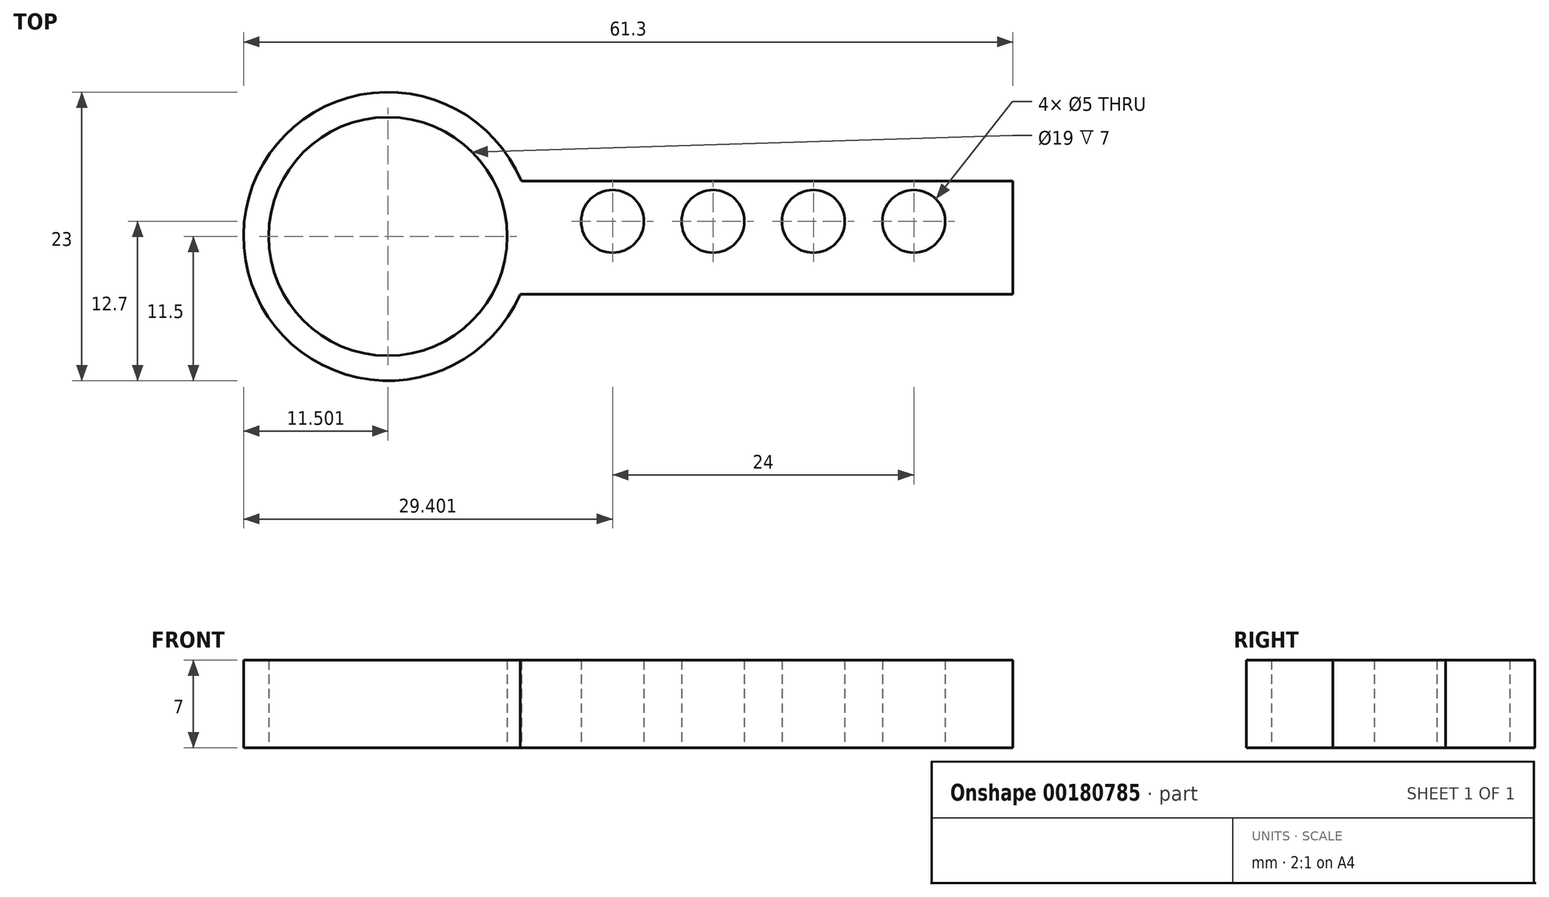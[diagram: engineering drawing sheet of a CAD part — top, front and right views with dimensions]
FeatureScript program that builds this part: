
annotation { "Feature Type Name" : "Feature", "Feature Type Description" : "" }
export const myFeature = defineFeature(function(context is Context, id is Id, definition is map)
    precondition{}
    {
        {
            var Q0;
            Q0=qCreatedBy(makeId("Top.planeOp"),FACE);
            var sketch = newSketch(context, id + "F0", { "sketchPlane" : qUnion([Q0])});
            skLineSegment(sketch, "E0.bottom", {"start": v(-51.54, 17.4) * mm, "end": v(-11.74, 17.4) * mm});
            skLineSegment(sketch, "E0.top", {"start": v(-51.54, 8.4) * mm, "end": v(-11.74, 8.4) * mm});
            skLineSegment(sketch, "E0.left", {"start": v(-51.54, 17.4) * mm, "end": v(-51.54, 8.4) * mm});
            skLineSegment(sketch, "E0.right", {"start": v(-11.74, 17.4) * mm, "end": v(-11.74, 8.4) * mm});
            skCircle(sketch, "E1", {"center": v(-43.64, 14.2) * mm, "radius": 2.5 * mm});
            skCircle(sketch, "E2.1.0.0", {"center": v(-35.64, 14.2) * mm, "radius": 2.5 * mm});
            skCircle(sketch, "E2.2.0.0", {"center": v(-27.64, 14.2) * mm, "radius": 2.5 * mm});
            skCircle(sketch, "E2.3.0.0", {"center": v(-19.64, 14.2) * mm, "radius": 2.5 * mm});
            skLineSegment(sketch, "E2.direction1", {"start": v(-43.64, 14.2) * mm, "end": v(-35.64, 14.2) * mm, "construction": true});
            skCircle(sketch, "E3", {"center": v(-61.54, 13) * mm, "radius": 11.5 * mm});
            skCircle(sketch, "E4", {"center": v(-61.54, 13) * mm, "radius": 9.5 * mm});
            skSolve(sketch);
        }
        {
            var Q0;
            {var subQ0=sQuery(id+"F0.wireOp",EDGE,"E0.right");Q0=makeQuery(id+"F0.imprint","IMPRINT",FACE,{"disambiguationData":[TD([[makeQuery(id+"F0.imprint","IMPRINT",EDGE,{"derivedFrom":subQ0}),-1.0]])]});}
            var Q1;
            {var subQ5=sQuery(id+"F0.wireOp",EDGE,"E0.left");Q1=makeQuery(id+"F0.imprint","IMPRINT",FACE,{"disambiguationData":[TD([[makeQuery(id+"F0.imprint","IMPRINT",EDGE,{"derivedFrom":subQ5}),-1.0]])]});}
            var Q2;
            {var subQ0=sQuery(id+"F0.wireOp",EDGE,"E0.left");Q2=makeQuery(id+"F0.imprint","IMPRINT",FACE,{"disambiguationData":[TD([[makeQuery(id+"F0.imprint","IMPRINT",EDGE,{"derivedFrom":subQ0}),1.0]])]});}
            extrude(context, id + "F1", {"entities" : qUnion([Q0, Q1, Q2]), "depth" : 7 * mm});
        }
    });
